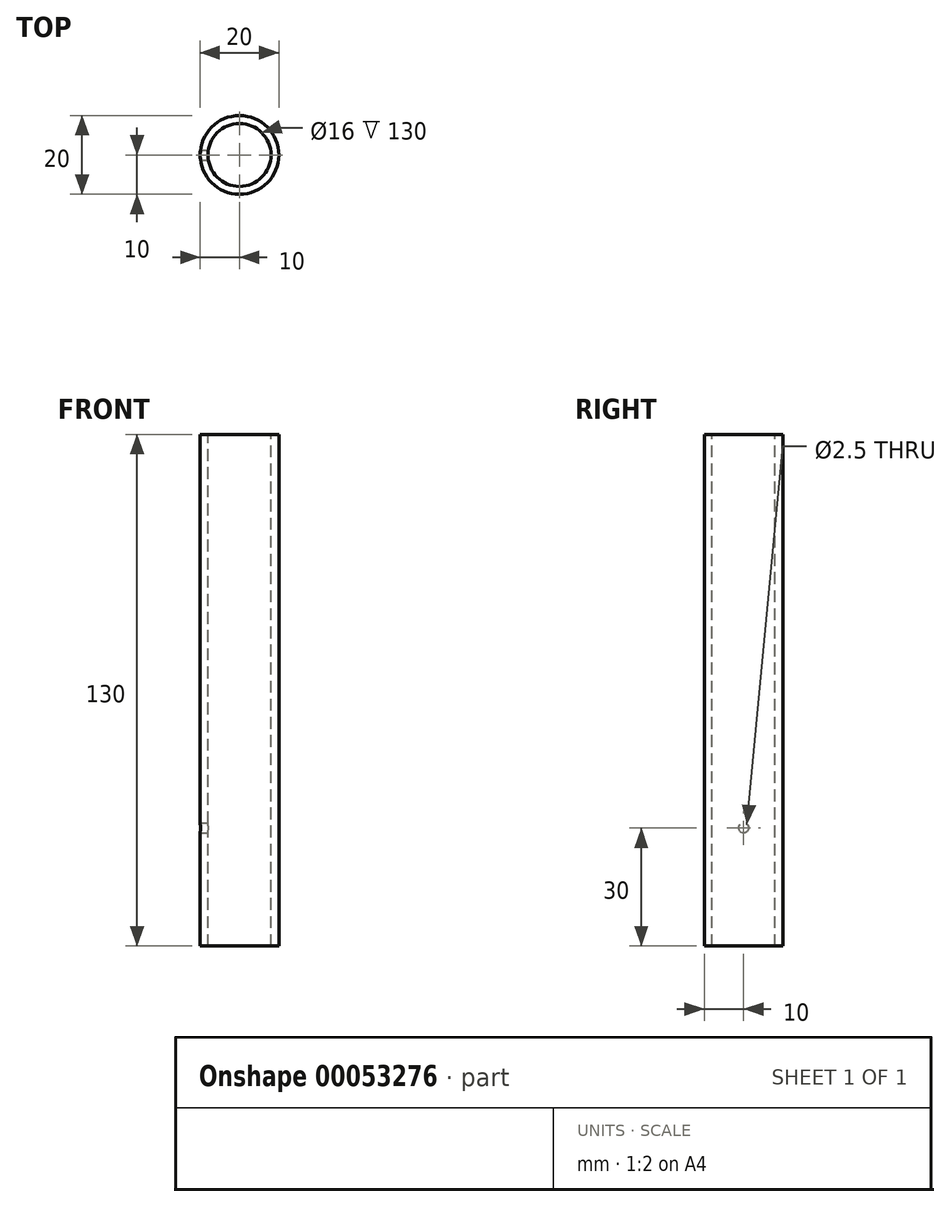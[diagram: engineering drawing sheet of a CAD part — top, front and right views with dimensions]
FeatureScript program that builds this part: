
annotation { "Feature Type Name" : "Feature", "Feature Type Description" : "" }
export const myFeature = defineFeature(function(context is Context, id is Id, definition is map)
    precondition{}
    {
        {
            var Q0;
            Q0=qCreatedBy(makeId("Top.planeOp"),FACE);
            var sketch = newSketch(context, id + "F0", { "sketchPlane" : qUnion([Q0])});
            skCircle(sketch, "E0", {"center": v(0, 0) * mm, "radius": 10 * mm});
            skSolve(sketch);
        }
        {
            var Q0;
            Q0=qCreatedBy(makeId("Top.planeOp"),FACE);
            cPlane(context, id + "F1", {"entities" : qUnion([Q0]), "cplaneType" : CPlaneType.OFFSET, "offset" : 60 * mm, "width" : 150 * mm, "height" : 150 * mm});
        }
        {
            var Q0;
            Q0=qCreatedBy(id+"F1.planeOp",FACE);
            var sketch = newSketch(context, id + "F2", { "sketchPlane" : qUnion([Q0])});
            skCircle(sketch, "E1", {"center": v(0, 0) * mm, "radius": 10 * mm});
            skSolve(sketch);
        }
        {
            var Q0;
            Q0 = qSketchRegion(id + "F0", true);
            var Q1;
            Q1 = qSketchRegion(id + "F2", true);
            loft(context, id + "F3", {"sheetProfilesArray" : [{ "sheetProfileEntities" : qUnion([Q0]) }, { "sheetProfileEntities" : qUnion([Q1]) }]});
        }
        {
            var Q0;
            Q0=qCreatedBy(makeId("Top.planeOp"),FACE);
            cPlane(context, id + "F4", {"entities" : qUnion([Q0]), "cplaneType" : CPlaneType.OFFSET, "offset" : 130 * mm, "width" : 150 * mm, "height" : 150 * mm});
        }
        {
            var Q0;
            Q0=qCreatedBy(id+"F4.planeOp",FACE);
            var sketch = newSketch(context, id + "F5", { "sketchPlane" : qUnion([Q0])});
            skCircle(sketch, "E2", {"center": v(0, 0) * mm, "radius": 10 * mm});
            skSolve(sketch);
        }
        {
            var Q1;
            Q1=makeQuery(id+"F3.opLoft","CAP_FACE",FACE,{"disambiguationData":[OSD([makeQuery(id+"F2.imprint","IMPRINT",FACE,{"disambiguationData":[TD([[makeQuery(id+"F2.imprint","IMPRINT",EDGE,{"derivedFrom":sQuery(id+"F2.wireOp",EDGE,"E1")}),1.0]])]})])],"isStart":true});
            var Q2;
            Q2=makeQuery(id+"F5.imprint","IMPRINT",FACE,{"disambiguationData":[TD([[makeQuery(id+"F5.imprint","IMPRINT",EDGE,{"derivedFrom":sQuery(id+"F5.wireOp",EDGE,"E2")}),1.0]])]});
            loft(context, id + "F6", {"operationType" : NewBodyOperationType.ADD, "sheetProfilesArray" : [{ "sheetProfileEntities" : qUnion([Q1]) }, { "sheetProfileEntities" : qUnion([Q2]) }]});
        }
        {
            var Q0;
            Q0=makeQuery(id+"F6.opLoft","CAP_FACE",FACE,{"disambiguationData":[OSD([makeQuery(id+"F5.imprint","IMPRINT",FACE,{"disambiguationData":[TD([[makeQuery(id+"F5.imprint","IMPRINT",EDGE,{"derivedFrom":sQuery(id+"F5.wireOp",EDGE,"E2")}),1.0]])]})])],"isStart":true});
            var sketch = newSketch(context, id + "F7", { "sketchPlane" : qUnion([Q0])});
            skCircle(sketch, "E3", {"center": v(0, 0) * mm, "radius": 10 * mm});
            skCircle(sketch, "E4", {"center": v(0, 0) * mm, "radius": 8 * mm});
            skSolve(sketch);
        }
        {
            var Q0;
            Q0=makeQuery(id+"F7.imprint","IMPRINT",FACE,{"disambiguationData":[TD([[makeQuery(id+"F7.imprint","IMPRINT",EDGE,{"derivedFrom":sQuery(id+"F7.wireOp",EDGE,"E4")}),1.0]])]});
            extrude(context, id + "F8", {"entities" : qUnion([Q0]), "operationType" : NewBodyOperationType.REMOVE, "endBound" : BoundingType.THROUGH_ALL, "oppositeDirection" : true, "depth" : 25 * mm});
        }
        {
            var Q0;
            Q0=qCreatedBy(makeId("Right.planeOp"),FACE);
            var sketch = newSketch(context, id + "F9", { "sketchPlane" : qUnion([Q0])});
            skLineSegment(sketch, "E5", {"start": v(0, 0) * mm, "end": v(0, 30) * mm});
            skCircle(sketch, "E6", {"center": v(0, 30) * mm, "radius": 1.25 * mm});
            skSolve(sketch);
        }
        {
            var Q0;
            Q0 = qSketchRegion(id + "F9", true);
            extrude(context, id + "F10", {"entities" : qUnion([Q0]), "operationType" : NewBodyOperationType.REMOVE, "endBound" : BoundingType.THROUGH_ALL, "oppositeDirection" : true, "depth" : 25 * mm});
        }
    });
